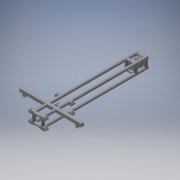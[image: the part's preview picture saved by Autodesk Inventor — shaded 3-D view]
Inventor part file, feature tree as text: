
AUTODESK INVENTOR PART (.ipt)
format: ipt  version: 2016 (Build 200138000, 138)  size: 566,784 bytes
history: native  units: in
note: dims shown in document units (in); Inventor stores cm internally (conversion verified against a paired STEP export)
features: sketch x17, extrude x15, plane x6, fillet x4, delete_face x4, projected_geometry x3, hole x2, other x2, mirror x1
ambient origin geometry x8: Origin, YZ Plane, XZ Plane, XY Plane, X Axis, Y Axis, Z Axis, Center Point
bodies: Solid1 (feature_tree)
feature tree (54):
  extrude  "Extrusion1"  Depth=6.0in
  sketch  "Sketch2"  dims[d6=2.0in d7=72.0in d8=0.0in]
  plane  "Work Plane1"
  extrude  "Extrusion2"  Depth=2.0in TaperAngle=0.0deg
  plane  "Work Plane2"
  extrude  "Extrusion3"  Depth=2.0in
  plane  "Work Plane3"
  extrude  "Extrusion4"  TaperAngle=90.0deg  [1 undecoded]
  extrude  "Extrusion5"  Depth=2.0in TaperAngle=0.0deg
  extrude  "Extrusion6"  Depth=2.0in
  fillet  "Fillet1"  Radius=2.0in
  extrude  "Extrusion7"  Depth=2.0in
  extrude  "Extrusion8"  Depth=2.0in
  mirror  "Mirror1"
  extrude  "Extrusion9"  Depth=2.0in
  extrude  "Extrusion10"  Depth=2.0in
  fillet  "Fillet2"  Radius=2.0in
  extrude  "Extrusion11"  Depth=3.0in TaperAngle=0.0deg
  delete_face  "Delete Face1"
  delete_face  "Delete Face2"
  delete_face  "Delete Face3"
  delete_face  "Delete Face4"
  plane  "Work Plane5"
  hole  "Hole1"  [1 undecoded]
  extrude  "Extrusion12"  Depth=3.0in TaperAngle=0.0deg
  extrude  "Extrusion13"  Depth=2.0in
  plane  "Work Plane6"
  extrude  "Extrusion14"  Depth=1.5in TaperAngle=0.0deg
  hole  "Hole3"  [1 undecoded]
  fillet  "Fillet3"  Radius=6.0in
  fillet  "Fillet4"  Radius=6.0in
  plane  "Work Plane7"
  extrude  "Extrusion15"  Depth=0.5in TaperAngle=0.0deg
  sketch  "Sketch1"  dims[d0=6.0in d1=6.0in]
  projected_geometry  "Projected Loop1"
  projected_geometry  "Projected Loop2"
  projected_geometry  "Projected Loop3"
  sketch  "Sketch3"  dims[d9=90.0deg d10=2.0in]
  sketch  "Sketch4"  dims[d11=6.0in d12=0.0in d13=90.0deg]
  sketch  "Sketch7"  dims[d14=2.0in d18=6.0in d19=0.0in]
  sketch  "Sketch9"  dims[d22=3.0in d23=2.0in d24=2.0in]
  sketch  "Sketch10"  dims[d25=42.0in d26=0.0in d27=2.0in]
  sketch  "Sketch11"  dims[d28=2.0in d29=2.0in]
  sketch  "Sketch12"  dims[d30=2.0in d31=18.0in]
  sketch  "Sketch13"  dims[d32=2.0in d33=2.0in d34=2.0in]
  sketch  "Sketch14"  dims[d35=2.0in d36=3.0in d37=0.0in]
  sketch  "Sketch15"  dims[d38=1.5in d39=0.0in d40=1.0in]
  sketch  "Sketch16"  dims[d41=3.0in d42=0.0in d43=3.0in d44=0.0in]
  sketch  "Sketch17"  dims[d49=2.0in d50=2.0in]
  sketch  "Sketch18"  dims[d51=2.0in d52=0.0in d53=1.5in d54=0.0in]
  other  "Work Axis1"
  other  "Work Axis2"
  sketch  "Sketch19"  dims[d55=1.0in d56=10.0in d57=0.0in d58=6.0in]
  sketch  "Sketch20"  dims[d59=6.0in d60=0.75in d61=0.375in d62=0.25in d63=0.5635in d64=6.0in d65=0.8108in d66=6.0in d67=8.0in d68=0.0in d78=6.0in d79=0.0in d80=6.0in d81=0.0in d82=1.0in d83=1.0in d84=5.5in d85=0.75in d86=0.375in d87=0.25in d88=0.5635in d89=7.5in d90=0.0in d91=0.125in d92=0.125in d93=1.0in d94=0.5in d95=0.5in d96=2.0in d97=0.5in d98=0.0in]
note: 3 required parameter values undecoded (feature->parameter linkage not recoverable at this tier; creation-order binding heuristic only, values carry confidence <= 0.55)
